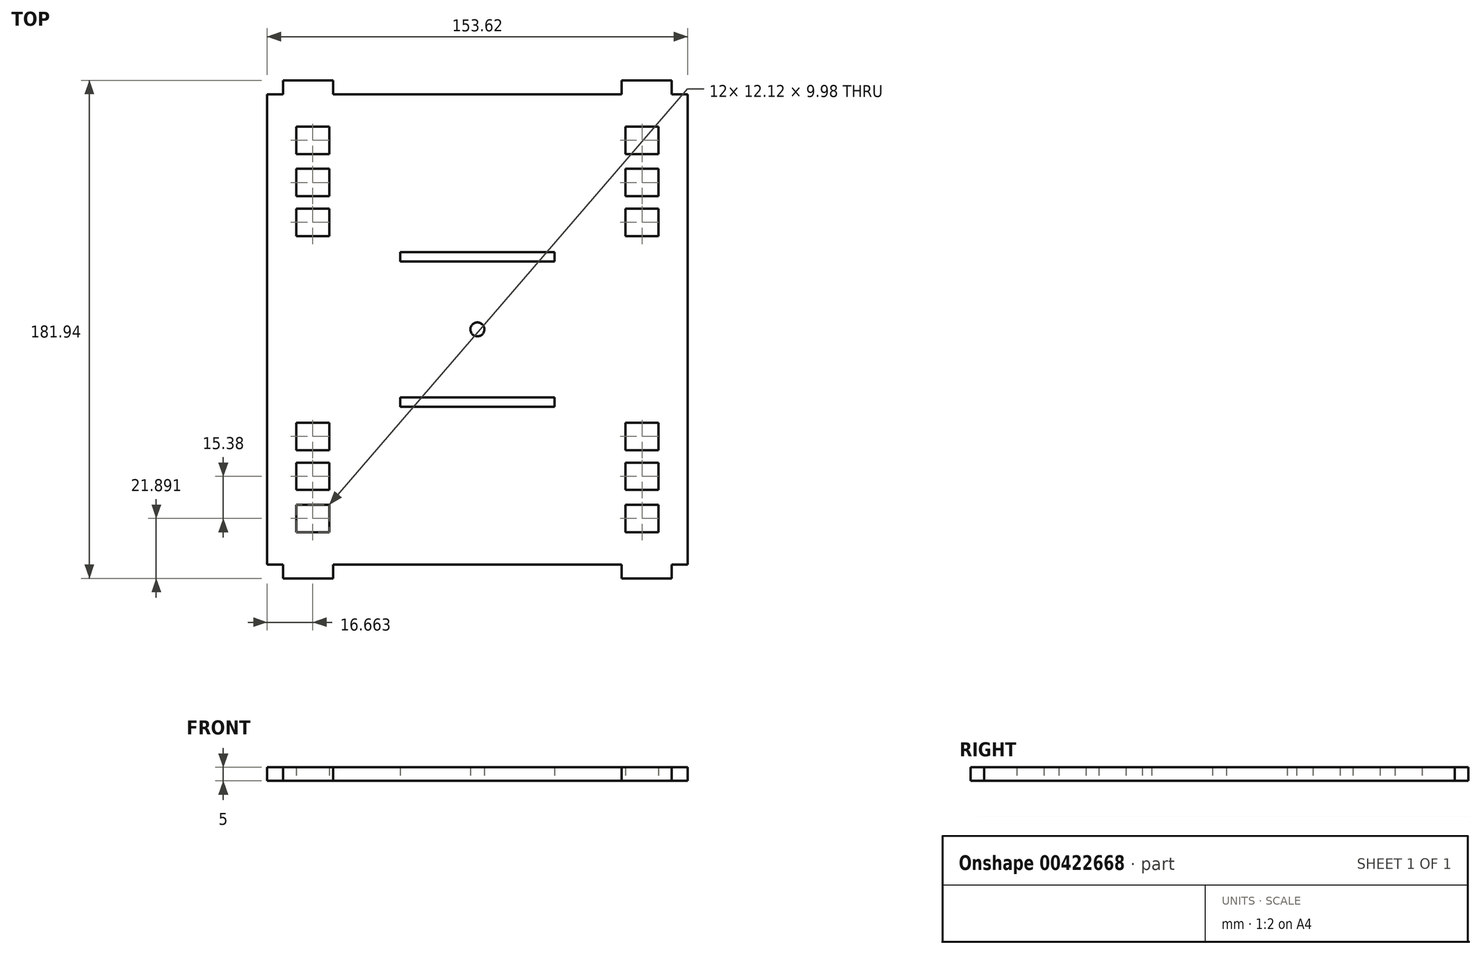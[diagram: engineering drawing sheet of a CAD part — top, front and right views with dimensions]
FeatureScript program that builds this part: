
annotation { "Feature Type Name" : "Feature", "Feature Type Description" : "" }
export const myFeature = defineFeature(function(context is Context, id is Id, definition is map)
    precondition{}
    {
        {
            var Q0;
            Q0=qCreatedBy(makeId("Top.planeOp"),FACE);
            var sketch = newSketch(context, id + "F0", { "sketchPlane" : qUnion([Q0])});
            skLineSegment(sketch, "E0", {"start": v(-121.43, 83.07) * mm, "end": v(-121.43, -88.87) * mm});
            skLineSegment(sketch, "E1", {"start": v(-121.43, -88.87) * mm, "end": v(32.19, -88.87) * mm});
            skLineSegment(sketch, "E2", {"start": v(32.19, -88.87) * mm, "end": v(32.19, 83.07) * mm});
            skLineSegment(sketch, "E3", {"start": v(32.19, 83.07) * mm, "end": v(-121.43, 83.07) * mm});
            skLineSegment(sketch, "E4", {"start": v(-121.43, 83.07) * mm, "end": v(-91.53, 83.07) * mm});
            skLineSegment(sketch, "E5.bottom", {"start": v(-115.62, 88.07) * mm, "end": v(-97.33, 88.07) * mm});
            skLineSegment(sketch, "E5.left", {"start": v(-115.62, 88.07) * mm, "end": v(-115.62, 78.07) * mm});
            skLineSegment(sketch, "E5.right", {"start": v(-97.33, 88.07) * mm, "end": v(-97.33, 78.07) * mm});
            skPoint(sketch, "E5.middle", {"position": v(-106.48, 83.07) * mm});
            skLineSegment(sketch, "E6", {"start": v(-121.43, -2.9) * mm, "end": v(32.19, -2.9) * mm, "construction": true});
            skLineSegment(sketch, "E7", {"start": v(-44.62, 83.07) * mm, "end": v(-44.62, -88.87) * mm, "construction": true});
            skPoint(sketch, "E8.MirrorP", {"position": v(17.24, 83.07) * mm});
            skLineSegment(sketch, "E9.MirrorCS", {"start": v(26.38, 88.07) * mm, "end": v(26.38, 78.07) * mm});
            skLineSegment(sketch, "E10.MirrorCS", {"start": v(8.1, 88.07) * mm, "end": v(8.1, 78.07) * mm});
            skLineSegment(sketch, "E11.MirrorCS", {"start": v(26.38, 88.07) * mm, "end": v(8.1, 88.07) * mm});
            skLineSegment(sketch, "E12.MirrorCS", {"start": v(26.38, -93.87) * mm, "end": v(8.1, -93.87) * mm});
            skPoint(sketch, "E13.MirrorP", {"position": v(17.24, -88.87) * mm});
            skLineSegment(sketch, "E14.MirrorCS", {"start": v(26.38, -93.87) * mm, "end": v(26.38, -83.87) * mm});
            skLineSegment(sketch, "E15.MirrorCS", {"start": v(8.1, -93.87) * mm, "end": v(8.1, -83.87) * mm});
            skPoint(sketch, "E16.MirrorP", {"position": v(-106.48, -88.87) * mm});
            skLineSegment(sketch, "E17.MirrorCS", {"start": v(-115.62, -93.87) * mm, "end": v(-97.33, -93.87) * mm});
            skLineSegment(sketch, "E18.MirrorCS", {"start": v(-115.62, -93.87) * mm, "end": v(-115.62, -83.87) * mm});
            skLineSegment(sketch, "E19.MirrorCS", {"start": v(-97.33, -93.87) * mm, "end": v(-97.33, -83.87) * mm});
            skLineSegment(sketch, "E20.bottom", {"start": v(-98.7, 61.19) * mm, "end": v(-110.82, 61.19) * mm});
            skLineSegment(sketch, "E20.top", {"start": v(-98.7, 71.17) * mm, "end": v(-110.82, 71.17) * mm});
            skLineSegment(sketch, "E20.left", {"start": v(-98.7, 61.19) * mm, "end": v(-98.7, 71.17) * mm});
            skLineSegment(sketch, "E20.right", {"start": v(-110.82, 61.19) * mm, "end": v(-110.82, 71.17) * mm});
            skPoint(sketch, "E20.middle", {"position": v(-104.77, 66.18) * mm});
            skLineSegment(sketch, "E21.bottom", {"start": v(-98.7, 45.8) * mm, "end": v(-110.82, 45.8) * mm});
            skLineSegment(sketch, "E21.top", {"start": v(-98.7, 55.79) * mm, "end": v(-110.82, 55.79) * mm});
            skLineSegment(sketch, "E21.left", {"start": v(-98.7, 45.8) * mm, "end": v(-98.7, 55.79) * mm});
            skLineSegment(sketch, "E21.right", {"start": v(-110.82, 45.8) * mm, "end": v(-110.82, 55.79) * mm});
            skPoint(sketch, "E21.middle", {"position": v(-104.77, 50.8) * mm});
            skLineSegment(sketch, "E22.bottom", {"start": v(-98.7, 31.23) * mm, "end": v(-110.82, 31.23) * mm});
            skLineSegment(sketch, "E22.top", {"start": v(-98.7, 41.21) * mm, "end": v(-110.82, 41.21) * mm});
            skLineSegment(sketch, "E22.left", {"start": v(-98.7, 31.23) * mm, "end": v(-98.7, 41.21) * mm});
            skLineSegment(sketch, "E22.right", {"start": v(-110.82, 31.23) * mm, "end": v(-110.82, 41.21) * mm});
            skPoint(sketch, "E22.middle", {"position": v(-104.77, 36.22) * mm});
            skLineSegment(sketch, "E23.MirrorCS", {"start": v(9.47, 41.21) * mm, "end": v(21.59, 41.21) * mm});
            skLineSegment(sketch, "E24.MirrorCS", {"start": v(21.59, 61.19) * mm, "end": v(21.59, 71.17) * mm});
            skLineSegment(sketch, "E25.MirrorCS", {"start": v(9.47, 45.8) * mm, "end": v(9.47, 55.79) * mm});
            skPoint(sketch, "E26.MirrorP", {"position": v(15.53, 66.18) * mm});
            skPoint(sketch, "E27.MirrorP", {"position": v(15.53, 50.8) * mm});
            skLineSegment(sketch, "E28.MirrorCS", {"start": v(21.59, 45.8) * mm, "end": v(21.59, 55.79) * mm});
            skPoint(sketch, "E29.MirrorP", {"position": v(15.53, 36.22) * mm});
            skLineSegment(sketch, "E30.MirrorCS", {"start": v(21.59, 31.23) * mm, "end": v(21.59, 41.21) * mm});
            skLineSegment(sketch, "E31.MirrorCS", {"start": v(9.47, 61.19) * mm, "end": v(9.47, 71.17) * mm});
            skLineSegment(sketch, "E32.MirrorCS", {"start": v(9.47, 61.19) * mm, "end": v(21.59, 61.19) * mm});
            skLineSegment(sketch, "E33.MirrorCS", {"start": v(9.47, 55.79) * mm, "end": v(21.59, 55.79) * mm});
            skLineSegment(sketch, "E34.MirrorCS", {"start": v(9.47, 45.8) * mm, "end": v(21.59, 45.8) * mm});
            skLineSegment(sketch, "E35.MirrorCS", {"start": v(9.47, 71.17) * mm, "end": v(21.59, 71.17) * mm});
            skLineSegment(sketch, "E36.MirrorCS", {"start": v(9.47, 31.23) * mm, "end": v(9.47, 41.21) * mm});
            skLineSegment(sketch, "E37.MirrorCS", {"start": v(9.47, 31.23) * mm, "end": v(21.59, 31.23) * mm});
            skLineSegment(sketch, "E38.MirrorCS", {"start": v(9.47, -37.04) * mm, "end": v(21.59, -37.04) * mm});
            skLineSegment(sketch, "E39.MirrorCS", {"start": v(21.59, -51.6) * mm, "end": v(21.59, -61.59) * mm});
            skLineSegment(sketch, "E40.MirrorCS", {"start": v(9.47, -47.01) * mm, "end": v(21.59, -47.01) * mm});
            skLineSegment(sketch, "E41.MirrorCS", {"start": v(9.47, -61.59) * mm, "end": v(21.59, -61.59) * mm});
            skLineSegment(sketch, "E42.MirrorCS", {"start": v(9.47, -37.04) * mm, "end": v(9.47, -47.01) * mm});
            skPoint(sketch, "E43.MirrorP", {"position": v(15.53, -42.02) * mm});
            skLineSegment(sketch, "E44.MirrorCS", {"start": v(9.47, -51.6) * mm, "end": v(9.47, -61.59) * mm});
            skLineSegment(sketch, "E45.MirrorCS", {"start": v(9.47, -66.99) * mm, "end": v(21.59, -66.99) * mm});
            skLineSegment(sketch, "E46.MirrorCS", {"start": v(21.59, -37.04) * mm, "end": v(21.59, -47.01) * mm});
            skLineSegment(sketch, "E47.MirrorCS", {"start": v(9.47, -66.99) * mm, "end": v(9.47, -76.97) * mm});
            skLineSegment(sketch, "E48.MirrorCS", {"start": v(21.59, -66.99) * mm, "end": v(21.59, -76.97) * mm});
            skLineSegment(sketch, "E49.MirrorCS", {"start": v(9.47, -76.97) * mm, "end": v(21.59, -76.97) * mm});
            skPoint(sketch, "E50.MirrorP", {"position": v(15.53, -71.98) * mm});
            skPoint(sketch, "E51.MirrorP", {"position": v(15.53, -56.6) * mm});
            skLineSegment(sketch, "E52.MirrorCS", {"start": v(9.47, -51.6) * mm, "end": v(21.59, -51.6) * mm});
            skLineSegment(sketch, "E53.MirrorCS", {"start": v(-110.82, -66.99) * mm, "end": v(-110.82, -76.97) * mm});
            skLineSegment(sketch, "E54.MirrorCS", {"start": v(-98.7, -51.6) * mm, "end": v(-98.7, -61.59) * mm});
            skLineSegment(sketch, "E55.MirrorCS", {"start": v(-110.82, -37.04) * mm, "end": v(-110.82, -47.01) * mm});
            skLineSegment(sketch, "E56.MirrorCS", {"start": v(-110.82, -51.6) * mm, "end": v(-110.82, -61.59) * mm});
            skLineSegment(sketch, "E57.MirrorCS", {"start": v(-98.7, -66.99) * mm, "end": v(-110.82, -66.99) * mm});
            skPoint(sketch, "E58.MirrorP", {"position": v(-104.77, -71.98) * mm});
            skLineSegment(sketch, "E59.MirrorCS", {"start": v(-98.7, -37.04) * mm, "end": v(-98.7, -47.01) * mm});
            skPoint(sketch, "E60.MirrorP", {"position": v(-104.77, -42.02) * mm});
            skLineSegment(sketch, "E61.MirrorCS", {"start": v(-98.7, -66.99) * mm, "end": v(-98.7, -76.97) * mm});
            skPoint(sketch, "E62.MirrorP", {"position": v(-104.77, -56.6) * mm});
            skLineSegment(sketch, "E63.MirrorCS", {"start": v(-98.7, -61.59) * mm, "end": v(-110.82, -61.59) * mm});
            skLineSegment(sketch, "E64.MirrorCS", {"start": v(-98.7, -76.97) * mm, "end": v(-110.82, -76.97) * mm});
            skLineSegment(sketch, "E65.MirrorCS", {"start": v(-98.7, -51.6) * mm, "end": v(-110.82, -51.6) * mm});
            skLineSegment(sketch, "E66.MirrorCS", {"start": v(-98.7, -47.01) * mm, "end": v(-110.82, -47.01) * mm});
            skLineSegment(sketch, "E67.MirrorCS", {"start": v(-98.7, -37.04) * mm, "end": v(-110.82, -37.04) * mm});
            skLineSegment(sketch, "E68.bottom", {"start": v(-16.43, 25.3) * mm, "end": v(-72.8, 25.3) * mm});
            skLineSegment(sketch, "E68.top", {"start": v(-16.43, 21.92) * mm, "end": v(-72.8, 21.92) * mm});
            skLineSegment(sketch, "E68.left", {"start": v(-16.43, 25.3) * mm, "end": v(-16.43, 21.92) * mm});
            skLineSegment(sketch, "E68.right", {"start": v(-72.8, 25.3) * mm, "end": v(-72.8, 21.92) * mm});
            skPoint(sketch, "E68.middle", {"position": v(-44.62, 23.61) * mm});
            skLineSegment(sketch, "E69.MirrorCS", {"start": v(-16.43, -31.11) * mm, "end": v(-16.43, -27.72) * mm});
            skLineSegment(sketch, "E70.MirrorCS", {"start": v(-72.8, -31.11) * mm, "end": v(-72.8, -27.72) * mm});
            skLineSegment(sketch, "E71.MirrorCS", {"start": v(-16.43, -27.72) * mm, "end": v(-72.8, -27.72) * mm});
            skLineSegment(sketch, "E72.MirrorCS", {"start": v(-16.43, -31.11) * mm, "end": v(-72.8, -31.11) * mm});
            skPoint(sketch, "E73.MirrorP", {"position": v(-44.62, -29.42) * mm});
            skCircle(sketch, "E74", {"center": v(-44.62, -2.9) * mm, "radius": 2.54 * mm});
            skSolve(sketch);
        }
        {
            var Q0;
            Q0 = qSketchRegion(id + "F0", true);
            extrude(context, id + "F1", {"entities" : qUnion([Q0]), "depth" : 5 * mm});
        }
    });
